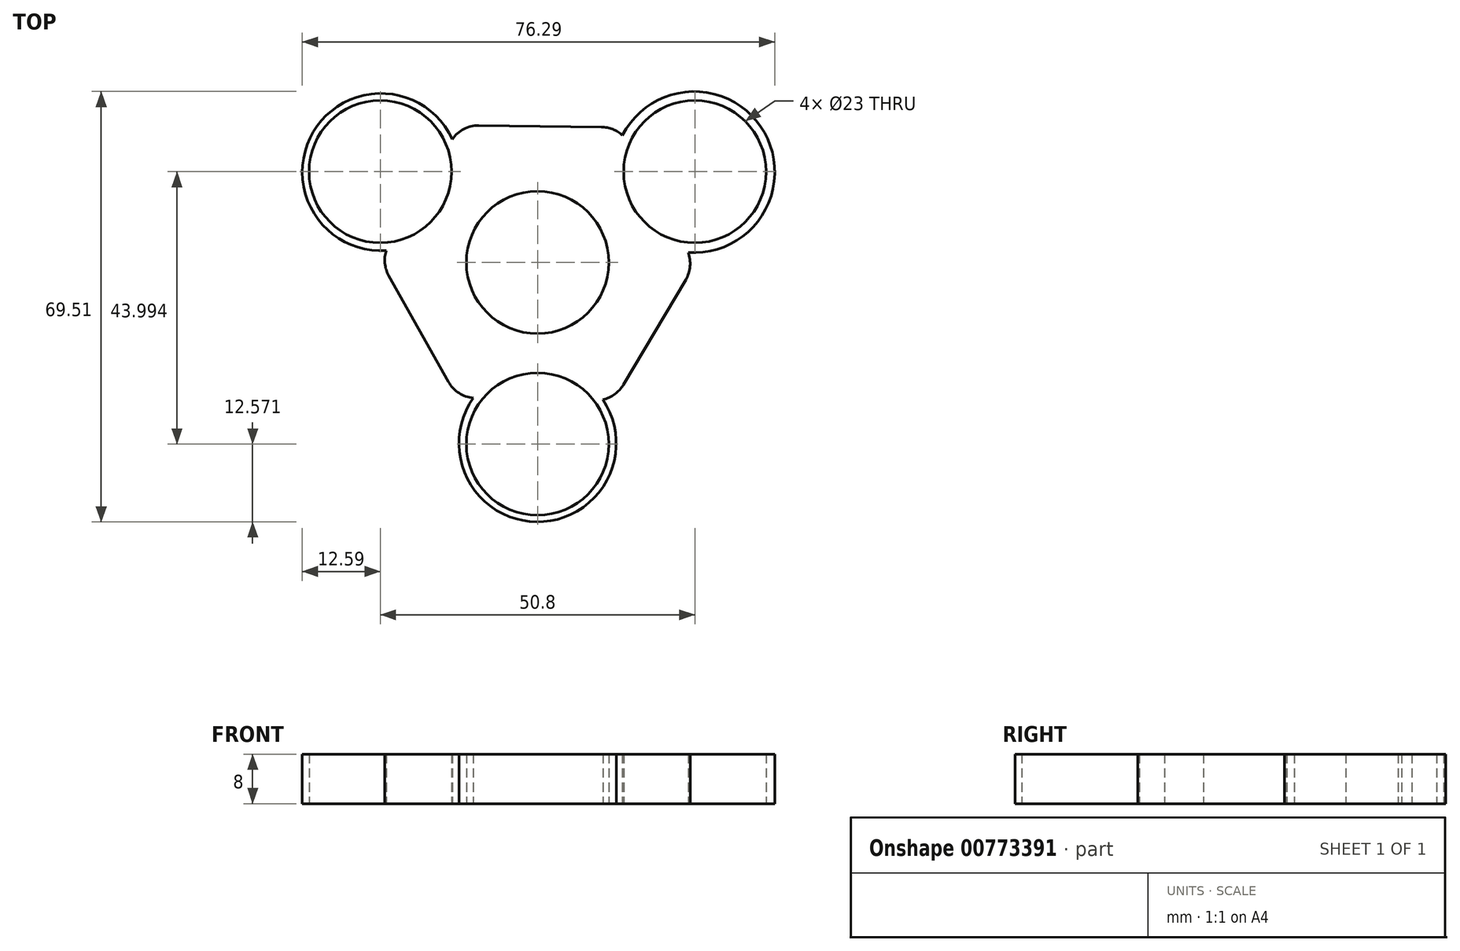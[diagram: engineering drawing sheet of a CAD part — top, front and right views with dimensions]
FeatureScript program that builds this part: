
annotation { "Feature Type Name" : "Feature", "Feature Type Description" : "" }
export const myFeature = defineFeature(function(context is Context, id is Id, definition is map)
    precondition{}
    {
        {
            var Q0;
            Q0=qCreatedBy(makeId("Top.planeOp"),FACE);
            var sketch = newSketch(context, id + "F0", { "sketchPlane" : qUnion([Q0])});
            skCircle(sketch, "E0", {"center": v(-25.4, 14.66) * mm, "radius": 11.5 * mm});
            skCircle(sketch, "E1", {"center": v(25.4, 14.66) * mm, "radius": 11.5 * mm});
            skCircle(sketch, "E2", {"center": v(0, -29.33) * mm, "radius": 11.5 * mm});
            skCircle(sketch, "E3", {"center": v(0, 0) * mm, "radius": 11.5 * mm});
            skSolve(sketch);
        }
        {
            var Q0;
            Q0=qCreatedBy(makeId("Top.planeOp"),FACE);
            var sketch = newSketch(context, id + "F1", { "sketchPlane" : qUnion([Q0])});
            skCircle(sketch, "E4", {"center": v(-25.29, 14.6) * mm, "radius": 12.7 * mm});
            skCircle(sketch, "E5", {"center": v(25.29, 14.6) * mm, "radius": 13 * mm});
            skCircle(sketch, "E6", {"center": v(0, -29.2) * mm, "radius": 12.7 * mm});
            skCircle(sketch, "E7.cCircle", {"center": v(0, 0) * mm, "radius": 22 * mm, "construction": true});
            skLineSegment(sketch, "E7.0", {"start": v(25.4, -0.3) * mm, "end": v(12.43, -22.15) * mm});
            skLineSegment(sketch, "E7.1", {"start": v(12.43, -22.15) * mm, "end": v(-12.96, -21.84) * mm});
            skLineSegment(sketch, "E7.2", {"start": v(-12.96, -21.84) * mm, "end": v(-25.4, 0.3) * mm});
            skLineSegment(sketch, "E7.3", {"start": v(-25.4, 0.3) * mm, "end": v(-12.43, 22.15) * mm});
            skLineSegment(sketch, "E7.4", {"start": v(-12.43, 22.15) * mm, "end": v(12.96, 21.84) * mm});
            skLineSegment(sketch, "E7.5", {"start": v(12.96, 21.84) * mm, "end": v(25.4, -0.3) * mm});
            skPoint(sketch, "E7.0.midPoint", {"position": v(18.92, -11.23) * mm});
            skSolve(sketch);
        }
        {
            var Q0;
            Q0 = qSketchRegion(id + "F1", true);
            extrude(context, id + "F2", {"entities" : qUnion([Q0]), "endBound" : BoundingType.SYMMETRIC, "depth" : 8 * mm, "offsetDistance" : 25.4 * mm});
        }
        {
            var Q0;
            Q0 = qSketchRegion(id + "F0", true);
            extrude(context, id + "F3", {"entities" : qUnion([Q0]), "operationType" : NewBodyOperationType.REMOVE, "endBound" : BoundingType.SYMMETRIC, "depth" : 8 * mm, "offsetDistance" : 25.4 * mm});
        }
        {
            var Q0;
            Q0=makeQuery(id+"F2.opExtrude","SWEPT_EDGE",EDGE,{"disambiguationData":[OSD([sQuery(id+"F1.wireOp",EDGE,"E7.0"),sQuery(id+"F1.wireOp",EDGE,"E7.1")])]});
            var Q1;
            Q1=makeQuery(id+"F2.opExtrude","SWEPT_EDGE",EDGE,{"disambiguationData":[OSD([sQuery(id+"F1.wireOp",EDGE,"E7.0"),sQuery(id+"F1.wireOp",EDGE,"E7.5")])]});
            var Q2;
            Q2=makeQuery(id+"F2.opExtrude","SWEPT_EDGE",EDGE,{"disambiguationData":[OSD([sQuery(id+"F1.wireOp",EDGE,"E7.4"),sQuery(id+"F1.wireOp",EDGE,"E7.5")])]});
            var Q3;
            Q3=makeQuery(id+"F2.opExtrude","SWEPT_EDGE",EDGE,{"disambiguationData":[OSD([sQuery(id+"F1.wireOp",EDGE,"E7.3"),sQuery(id+"F1.wireOp",EDGE,"E7.4")])]});
            var Q4;
            Q4=makeQuery(id+"F2.opExtrude","SWEPT_EDGE",EDGE,{"disambiguationData":[OSD([sQuery(id+"F1.wireOp",EDGE,"E7.1"),sQuery(id+"F1.wireOp",EDGE,"E7.2")])]});
            var Q5;
            Q5=makeQuery(id+"F2.opExtrude","SWEPT_EDGE",EDGE,{"disambiguationData":[OSD([sQuery(id+"F1.wireOp",EDGE,"E7.2"),sQuery(id+"F1.wireOp",EDGE,"E7.3")])]});
            fillet(context, id + "F4", {"entities" : qUnion([Q0, Q1, Q2, Q3, Q4, Q5]), "radius" : 5.08 * mm, "tangentPropagation" : true, "allowEdgeOverflow" : false});
        }
    });
